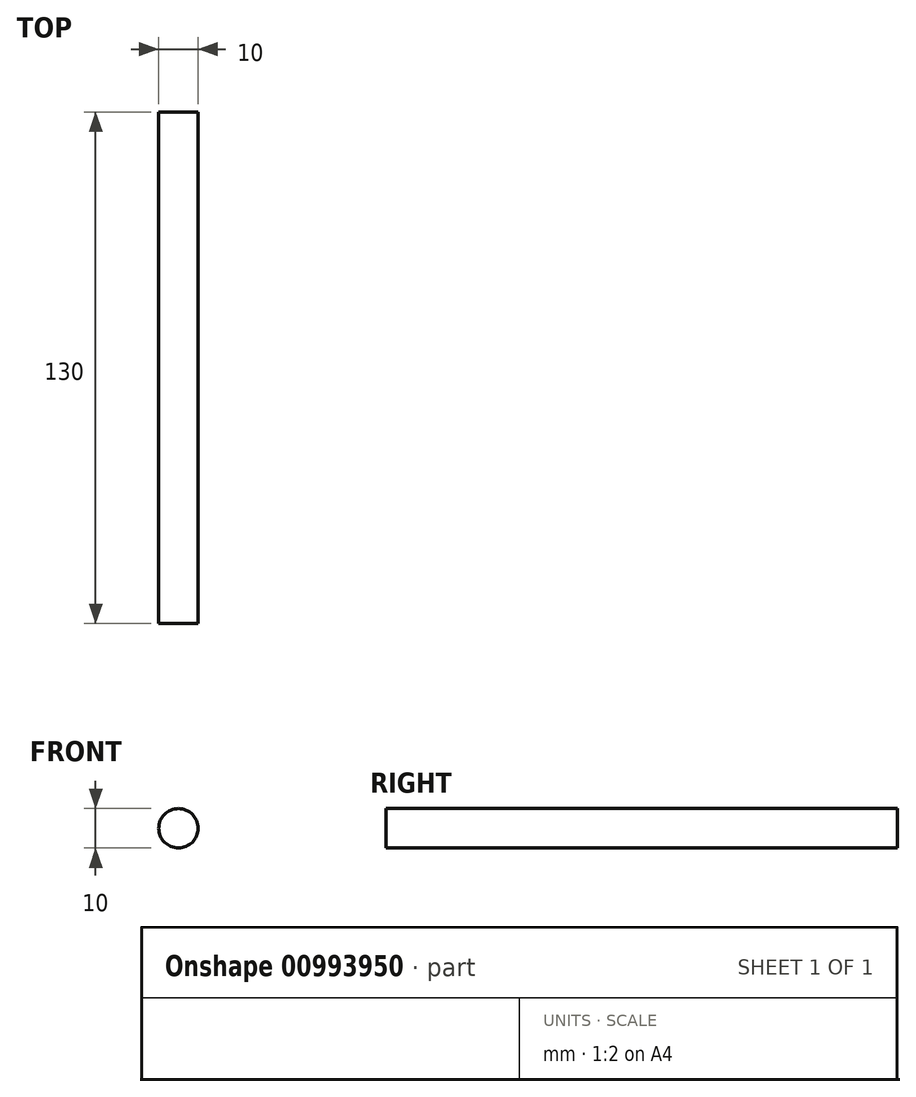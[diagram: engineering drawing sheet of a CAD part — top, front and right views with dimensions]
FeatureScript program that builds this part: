
annotation { "Feature Type Name" : "Feature", "Feature Type Description" : "" }
export const myFeature = defineFeature(function(context is Context, id is Id, definition is map)
    precondition{}
    {
        {
            var Q0;
            Q0=qCreatedBy(makeId("Front.planeOp"),FACE);
            var sketch = newSketch(context, id + "F0", { "sketchPlane" : qUnion([Q0])});
            skCircle(sketch, "E0", {"center": v(0, 0) * mm, "radius": 5 * mm});
            skSolve(sketch);
        }
        {
            var Q0;
            Q0 = qSketchRegion(id + "F0", true);
            extrude(context, id + "F1", {"entities" : qUnion([Q0]), "endBound" : BoundingType.SYMMETRIC, "depth" : 130 * mm, "offsetDistance" : 25 * mm});
        }
    });
